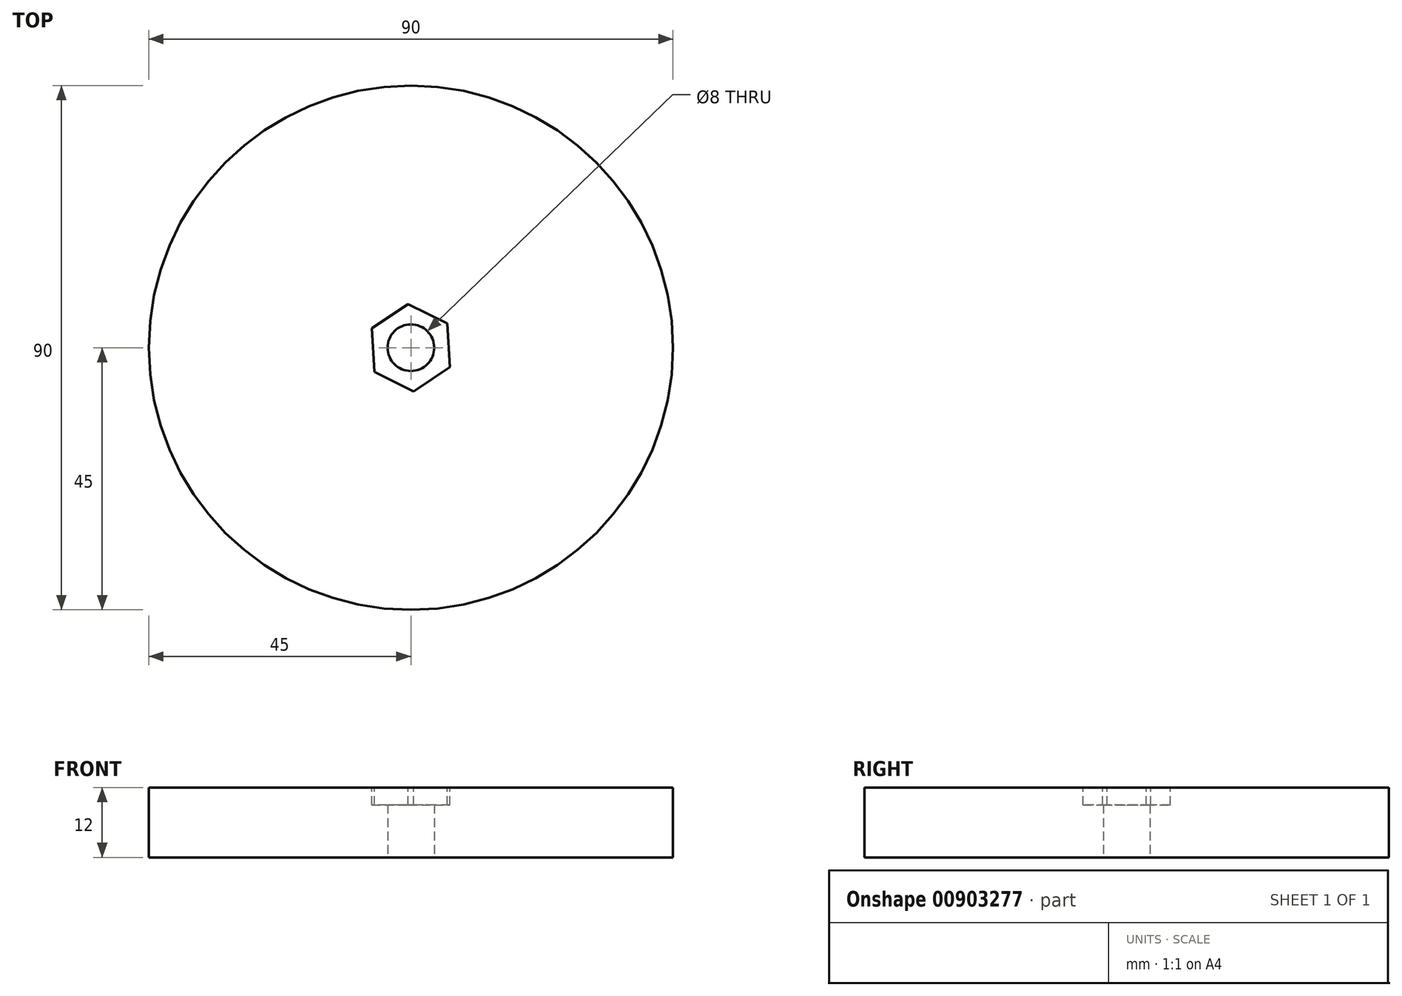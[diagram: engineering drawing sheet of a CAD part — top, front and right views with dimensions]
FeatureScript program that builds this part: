
annotation { "Feature Type Name" : "Feature", "Feature Type Description" : "" }
export const myFeature = defineFeature(function(context is Context, id is Id, definition is map)
    precondition{}
    {
        {
            var Q0;
            Q0=qCreatedBy(makeId("Top.planeOp"),FACE);
            var sketch = newSketch(context, id + "F0", { "sketchPlane" : qUnion([Q0])});
            skCircle(sketch, "E0", {"center": v(0, 0) * mm, "radius": 45 * mm});
            skCircle(sketch, "E1", {"center": v(0, 0) * mm, "radius": 4 * mm});
            skSolve(sketch);
        }
        {
            var Q0;
            Q0=makeQuery(id+"F0.imprint","IMPRINT",FACE,{"disambiguationData":[TD([[makeQuery(id+"F0.imprint","IMPRINT",EDGE,{"derivedFrom":sQuery(id+"F0.wireOp",EDGE,"E0")}),1.0]])]});
            extrude(context, id + "F1", {"entities" : qUnion([Q0]), "depth" : 12 * mm, "offsetDistance" : 25 * mm});
        }
        {
            var Q0;
            Q0=makeQuery(id+"F1.opExtrude","CAP_FACE",FACE,{"disambiguationData":[OSD([sQuery(id+"F0.wireOp",EDGE,"E0"),sQuery(id+"F0.wireOp",EDGE,"E1")])],"isStart":false});
            var sketch = newSketch(context, id + "F2", { "sketchPlane" : qUnion([Q0])});
            skCircle(sketch, "E2.cCircle", {"center": v(0, 0) * mm, "radius": 6.5 * mm, "construction": true});
            skLineSegment(sketch, "E2.0", {"start": v(6.72, -3.35) * mm, "end": v(0.46, -7.5) * mm});
            skLineSegment(sketch, "E2.1", {"start": v(0.46, -7.5) * mm, "end": v(-6.26, -4.14) * mm});
            skLineSegment(sketch, "E2.2", {"start": v(-6.26, -4.14) * mm, "end": v(-6.72, 3.35) * mm});
            skLineSegment(sketch, "E2.3", {"start": v(-6.72, 3.35) * mm, "end": v(-0.46, 7.5) * mm});
            skLineSegment(sketch, "E2.4", {"start": v(-0.46, 7.5) * mm, "end": v(6.26, 4.14) * mm});
            skLineSegment(sketch, "E2.5", {"start": v(6.26, 4.14) * mm, "end": v(6.72, -3.35) * mm});
            skPoint(sketch, "E2.0.midPoint", {"position": v(3.59, -5.42) * mm});
            skSolve(sketch);
        }
        {
            var Q0;
            Q0=makeQuery(id+"F2.imprint","IMPRINT",FACE,{"disambiguationData":[TD([[makeQuery(id+"F2.imprint","IMPRINT",EDGE,{"derivedFrom":sQuery(id+"F2.wireOp",EDGE,"E2.0")}),-1.0]])]});
            extrude(context, id + "F3", {"entities" : qUnion([Q0]), "operationType" : NewBodyOperationType.REMOVE, "oppositeDirection" : true, "depth" : 3 * mm, "offsetDistance" : 25 * mm});
        }
    });
